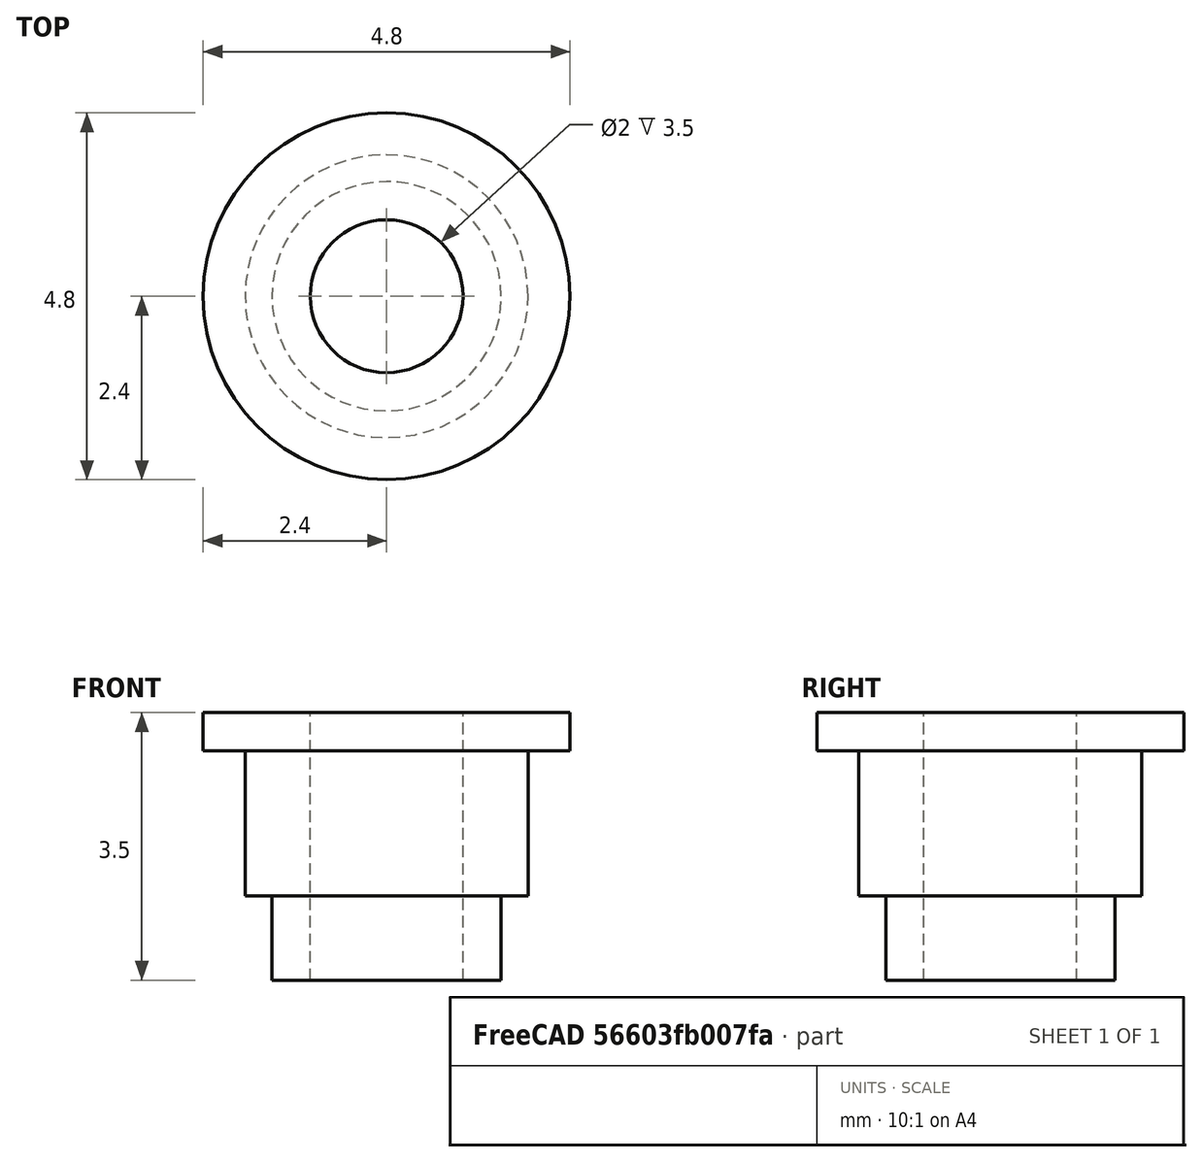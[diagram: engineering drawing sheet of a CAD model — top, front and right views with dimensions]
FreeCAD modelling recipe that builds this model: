
FCSTD DOCUMENT  (FreeCAD 1.0R39285 (Git))
Label: M2HeatSetInsert
License: All rights reserved
LicenseURL: https://en.wikipedia.org/wiki/All_rights_reserved
objects: App::Link×1, Sketcher::SketchObject×1, PartDesign::Revolution×1, PartDesign::Body×1
note: 6 computed .brp shape members not serialized (recipe doc carries the construction recipe); baked Part::Feature solids carry a one-line shape summary decoded from their .brp
EXTERNAL_REF file=../Dimentions.FCStd obj=dd004

FEATURE [App::Link] Link  label="M2HeatSetInsert"
  LinkedObject = -> <external ../Dimentions.FCStd>#dd004
FEATURE [Sketcher::SketchObject] Sketch001
  ArcFitTolerance = 1e-06
  AttachmentSupport = -> [XZ_Plane]
  FullyConstrained = true
  MakeInternals = true
  MapMode = 5
  Placement = pos=(0,0,0) rot=(1,0,0;1.5708rad)
  expr: Constraints[19] = <<M2HeatSetInsert>>.HoleDiameter
  expr: Constraints[20] = <<M2HeatSetInsert>>.CapDiameter / 2
  expr: Constraints[21] = <<M2HeatSetInsert>>.CapThickness
  expr: Constraints[22] = <<M2HeatSetInsert>>.BarbDiameter / 2
  expr: Constraints[23] = <<M2HeatSetInsert>>.BarbThickness
  expr: Constraints[24] = <<M2HeatSetInsert>>.TotalThickness
  expr: Constraints[25] = <<M2HeatSetInsert>>.InsetDiameter / 2
  sketch-geometry (9):
    g0: LineSegment StartX=1 StartY=1.75 StartZ=0 EndX=2.4 EndY=1.75 EndZ=0
    g1: LineSegment StartX=2.4 StartY=1.75 StartZ=0 EndX=2.4 EndY=1.25 EndZ=0
    g2: LineSegment StartX=2.4 StartY=1.25 StartZ=0 EndX=1.85 EndY=1.25 EndZ=0
    g3: LineSegment StartX=1.85 StartY=1.25 StartZ=0 EndX=1.85 EndY=-0.65 EndZ=0
    g4: LineSegment StartX=1.85 StartY=-0.65 StartZ=0 EndX=1.5 EndY=-0.65 EndZ=0
    g5: LineSegment StartX=1.5 StartY=-0.65 StartZ=0 EndX=1.5 EndY=-1.75 EndZ=0
    g6: LineSegment StartX=1.5 StartY=-1.75 StartZ=0 EndX=1 EndY=-1.75 EndZ=0
    g7: LineSegment StartX=1 StartY=-1.75 StartZ=0 EndX=1 EndY=1.75 EndZ=0
    g8: LineSegment [constr] StartX=-1 StartY=1.75 StartZ=0 EndX=-1 EndY=-1.75 EndZ=0
  constraints (26):
    c: Coincident(g0,g1)
    c: Coincident(g1,g2)
    c: Coincident(g2,g3)
    c: Coincident(g3,g4)
    c: Coincident(g4,g5)
    c: Coincident(g5,g6)
    c: Coincident(g6,g7)
    c: Coincident(g7,g0)
    c: Symmetric(g0,g6,g-1)
    c: Horizontal(g6)
    c: Horizontal(g0)
    c: Vertical(g5)
    c: Horizontal(g4)
    c: Vertical(g3)
    c: Horizontal(g2)
    c: Vertical(g1)
    c: Vertical(g8)
    c: Equal(g8,g7)
    c: Symmetric(g6,g8,g-2)
    c: DistanceX(g8,g0) = 2
    c: DistanceX(g-1,g0) = 2.4
    c: DistanceY(g1,g1) = 0.5
    c: DistanceX(g-1,g2) = 1.85
    c: DistanceY(g3,g3) = 1.9
    c: DistanceY(g7,g7) = 3.5
    c: DistanceX(g-1,g5) = 1.5
FEATURE [PartDesign::Revolution] Revolution
  Angle = 360
  Angle2 = 60
  Axis = (0,2e-16,1)
  Base = (0,0,0)
  Placement = pos=(0,0,0) rot=(1,0,0;1.5708rad)
  Profile = -> Sketch001
  ReferenceAxis = -> Sketch001 [V_Axis]
  Reversed = true
  Suppressed = false
  Type = 0
FEATURE [PartDesign::Body] Body  label="M2Insert"
  AllowCompound = false
  Group = -> [Sketch001,Revolution]
  Origin = -> Origin
  Tip = -> Revolution
